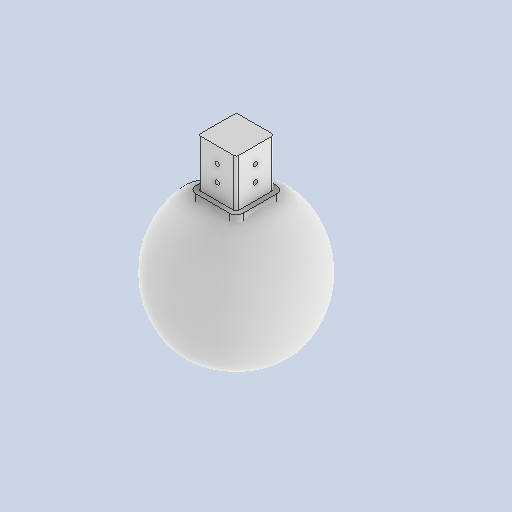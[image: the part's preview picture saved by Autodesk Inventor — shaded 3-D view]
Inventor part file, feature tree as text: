
AUTODESK INVENTOR PART (.ipt)
format: ipt  version: 2025 (Build 290162010, 162A)  size: 276,992 bytes
history: native  units: mm
features: sketch x4, extrude x2, hole x2, other x1
ambient origin geometry x8: Origin, YZ Plane, XZ Plane, XY Plane, X Axis, Y Axis, Z Axis, Center Point
bodies: Volumenkörper1 (feature_tree), Volumenkörper2 (feature_tree)
feature tree (9):
  extrude  "Extrusion1"  Depth=30.0mm TaperAngle=0.0deg
  other  "Form1"
  extrude  "Extrusion2"  [1 undecoded]
  hole  "Bohrung1"  [1 undecoded]
  hole  "Bohrung2"  [1 undecoded]
  sketch  "Skizze1"  dims[d0=50.0mm d1=0.0mm d2=30.0mm d3=0.0mm]
  sketch  "Skizze2"  dims[d4=1.8mm d5=6.0mm d6=3.023mm d7=2.0mm d8=14.3117mm d9=8.0mm d10=20.594885mm]
  sketch  "Skizze3"  dims[d11=1.8mm d12=6.0mm d13=4.0mm d14=2.0mm d15=90.0deg d16=8.0mm d17=20.594885mm]
  sketch  "Skizze4"
note: 3 required parameter values undecoded (feature->parameter linkage not recoverable at this tier; creation-order binding heuristic only, values carry confidence <= 0.55)
